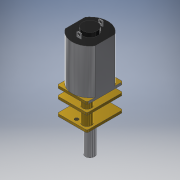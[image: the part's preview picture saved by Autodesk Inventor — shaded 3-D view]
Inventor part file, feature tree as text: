
AUTODESK INVENTOR PART (.ipt)
format: ipt  version: 2019.4 (Build 234330000, 330)  size: 287,744 bytes
history: native  units: mm
features: sketch x12, extrude x11, fillet x3, mirror x1, plane x1, hole x1
ambient origin geometry x8: Origin, YZ Plane, XZ Plane, XY Plane, X Axis, Y Axis, Z Axis, Center Point
bodies: Solid1 (feature_tree)
feature tree (29):
  extrude  "Extrusion1"  Depth=10.0mm
  extrude  "Extrusion2"  Depth=5.0mm
  extrude  "Extrusion3"  Depth=1.5mm
  extrude  "Extrusion4"  Depth=1.55mm
  fillet  "Fillet1"  Radius=1.65mm
  mirror  "Mirror1"
  extrude  "Extrusion5"  Depth=0.7mm
  extrude  "Extrusion6"  Depth=0.25mm
  plane  "Work Plane1"
  extrude  "Extrusion7"  Depth=0.8mm
  extrude  "Extrusion8"  Depth=2.15mm
  hole  "Hole1"  [1 undecoded]
  extrude  "Extrusion9"  Depth=8.2mm TaperAngle=0.0deg
  extrude  "Extrusion10"  Depth=0.8mm TaperAngle=0.0deg
  fillet  "Fillet2"  Radius=0.8mm
  fillet  "Fillet3"  Radius=4.5mm
  extrude  "Extrusion11"  Depth=0.5mm
  sketch  "Sketch1"  dims[d0=12.0mm d1=10.0mm]
  sketch  "Sketch2"  dims[d2=15.0mm d3=0.0mm d4=5.0mm]
  sketch  "Sketch3"  dims[d5=1.5mm d6=0.0mm d7=3.775mm]
  sketch  "Sketch4"  dims[d8=0.3mm d9=1.55mm d10=1.65mm d11=0.0mm]
  sketch  "Sketch5"  dims[d12=1.0mm d13=0.7mm]
  sketch  "Sketch6"  dims[d14=1.65mm d15=0.0mm d16=0.25mm]
  sketch  "Sketch7"  dims[d17=0.8mm d18=0.0mm d19=3.0mm]
  sketch  "Sketch8"  dims[d20=2.15mm d21=2.15mm]
  sketch  "Sketch9"  dims[d22=3.0mm d23=2.15mm]
  sketch  "Sketch10"  dims[d24=2.15mm d25=8.2mm d26=0.0mm]
  sketch  "Sketch11"  dims[d27=2.35mm d28=0.8mm d29=0.0mm d30=0.8mm d31=0.0mm d32=4.5mm]
  sketch  "Sketch12"  dims[d33=4.5mm d34=1.221mm d35=0.8mm d36=4.0mm d37=2.0mm d38=90.0deg d39=1.0mm d40=0.0mm d41=3.9mm d42=0.6mm d43=0.0mm d44=3.0mm d45=1.0mm d46=9.27mm d47=0.0mm d48=0.5mm d49=0.5mm d50=1.727mm d51=0.0mm]
note: 1 required parameter value undecoded (feature->parameter linkage not recoverable at this tier; creation-order binding heuristic only, values carry confidence <= 0.55)
